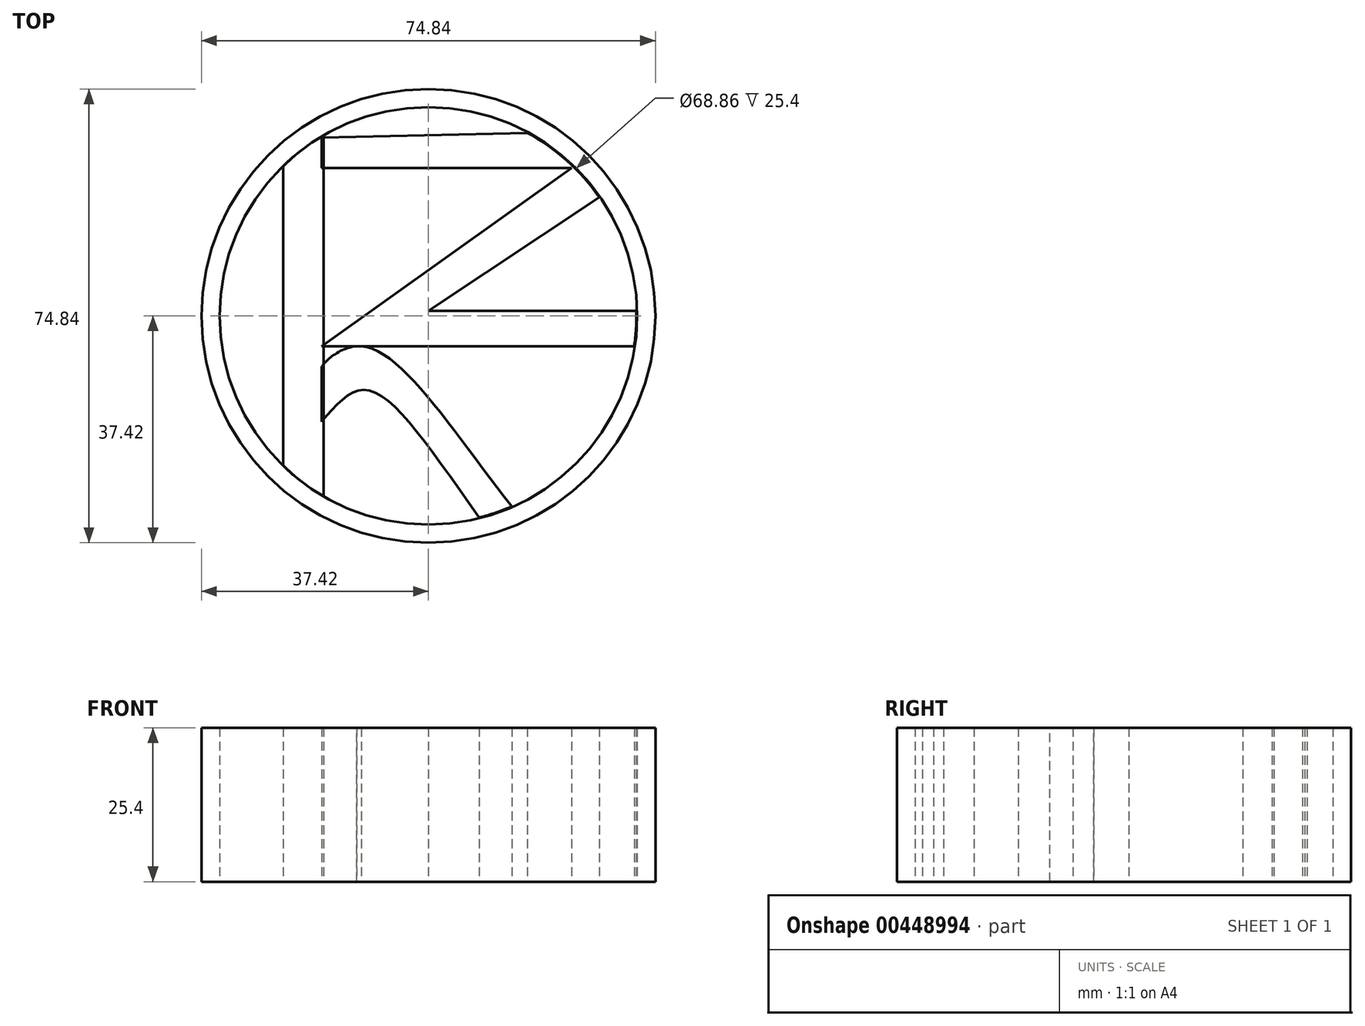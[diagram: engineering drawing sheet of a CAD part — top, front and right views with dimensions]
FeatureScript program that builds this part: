
annotation { "Feature Type Name" : "Feature", "Feature Type Description" : "" }
export const myFeature = defineFeature(function(context is Context, id is Id, definition is map)
    precondition{}
    {
        {
            var Q0;
            Q0=qCreatedBy(makeId("Top.planeOp"),FACE);
            var sketch = newSketch(context, id + "F0", { "sketchPlane" : qUnion([Q0])});
            skCircle(sketch, "E0", {"center": v(0, 0) * mm, "radius": 34.3 * mm});
            skCircle(sketch, "E1", {"center": v(0, 0) * mm, "radius": 36.17 * mm});
            skCircle(sketch, "E2", {"center": v(0, 0) * mm, "radius": 35.9 * mm});
            skCircle(sketch, "E3", {"center": v(0, 0) * mm, "radius": 36.09 * mm});
            skFitSpline(sketch, "E4", {"points": [v(8.4, -33.25) * mm, v(-10.39, -12.22) * mm, v(-17.62, -17.46) * mm], "startDerivative": vector(-39.38, 54.85) * mm, "endDerivative": vector(-19.95, -23.54) * mm});
            skFitSpline(sketch, "E5", {"points": [v(13.75, -31.42) * mm, v(-11.09, -5) * mm, v(-17.62, -8.43) * mm, v(-17.62, -10.5) * mm], "startDerivative": vector(-48.1, 60.5) * mm, "endDerivative": vector(1.93, -28.56) * mm});
            skLineSegment(sketch, "E6", {"start": v(-17.62, -29.43) * mm, "end": v(-17.62, 29.43) * mm});
            skLineSegment(sketch, "E7", {"start": v(-25.52, -22.91) * mm, "end": v(-25.52, 22.91) * mm});
            skLineSegment(sketch, "E8", {"start": v(-17.62, -5) * mm, "end": v(33.93, -5) * mm});
            skLineSegment(sketch, "E9", {"start": v(33.93, -5) * mm, "end": v(-17.62, -5) * mm});
            skLineSegment(sketch, "E10", {"start": v(-17.62, -5) * mm, "end": v(23.6, 24.4) * mm});
            skLineSegment(sketch, "E11", {"start": v(23.6, 24.4) * mm, "end": v(-17.62, 24.4) * mm});
            skLineSegment(sketch, "E12", {"start": v(34.29, 0.8) * mm, "end": v(0, 0.8) * mm});
            skLineSegment(sketch, "E13", {"start": v(0, 0.8) * mm, "end": v(28.16, 19.58) * mm});
            skLineSegment(sketch, "E14", {"start": v(16.3, 30.18) * mm, "end": v(-17.62, 29.43) * mm});
            skSolve(sketch);
        }
        {
            var Q0;
            {var subQ2=sQuery(id+"F0.wireOp",EDGE,"E10");Q0=makeQuery(id+"F0.imprint","IMPRINT",FACE,{"disambiguationData":[TD([[makeQuery(id+"F0.imprint","IMPRINT",EDGE,{"derivedFrom":subQ2}),-1.0]])]});}
            var Q1;
            {var subQ8=sQuery(id+"F0.wireOp",EDGE,"E4");Q1=makeQuery(id+"F0.imprint","IMPRINT",FACE,{"disambiguationData":[TD([[makeQuery(id+"F0.imprint","IMPRINT",EDGE,{"derivedFrom":subQ8}),-1.0]])]});}
            extrude(context, id + "F1", {"entities" : qUnion([Q0, Q1]), "depth" : 25.4 * mm});
        }
        {
            var Q0;
            Q0=qCreatedBy(makeId("Top.planeOp"),FACE);
            var sketch = newSketch(context, id + "F2", { "sketchPlane" : qUnion([Q0])});
            skCircle(sketch, "E15", {"center": v(0, 0) * mm, "radius": 34.43 * mm});
            skCircle(sketch, "E16", {"center": v(0, 0) * mm, "radius": 37.42 * mm});
            skLineSegment(sketch, "E17", {"start": v(-17.28, -29.78) * mm, "end": v(-17.28, 29.78) * mm});
            skLineSegment(sketch, "E18", {"start": v(-23.96, -24.72) * mm, "end": v(-23.96, 24.72) * mm});
            skSolve(sketch);
        }
        {
            var Q0;
            Q0 = qSketchRegion(id + "F2", true);
            extrude(context, id + "F3", {"entities" : qUnion([Q0]), "depth" : 25.4 * mm});
        }
        {
            var Q0;
            Q0 = qSketchRegion(id + "F2", true);
            extrude(context, id + "F4", {"entities" : qUnion([Q0]), "operationType" : NewBodyOperationType.ADD, "depth" : 25.4 * mm});
        }
        {
            var Q0;
            {var subQ0=sQuery(id+"F2.wireOp",EDGE,"E17");Q0=makeQuery(id+"F2.imprint","IMPRINT",FACE,{"disambiguationData":[TD([[makeQuery(id+"F2.imprint","IMPRINT",EDGE,{"derivedFrom":subQ0}),1.0]])]});}
            extrude(context, id + "F5", {"entities" : qUnion([Q0]), "depth" : 25.4 * mm});
        }
    });
